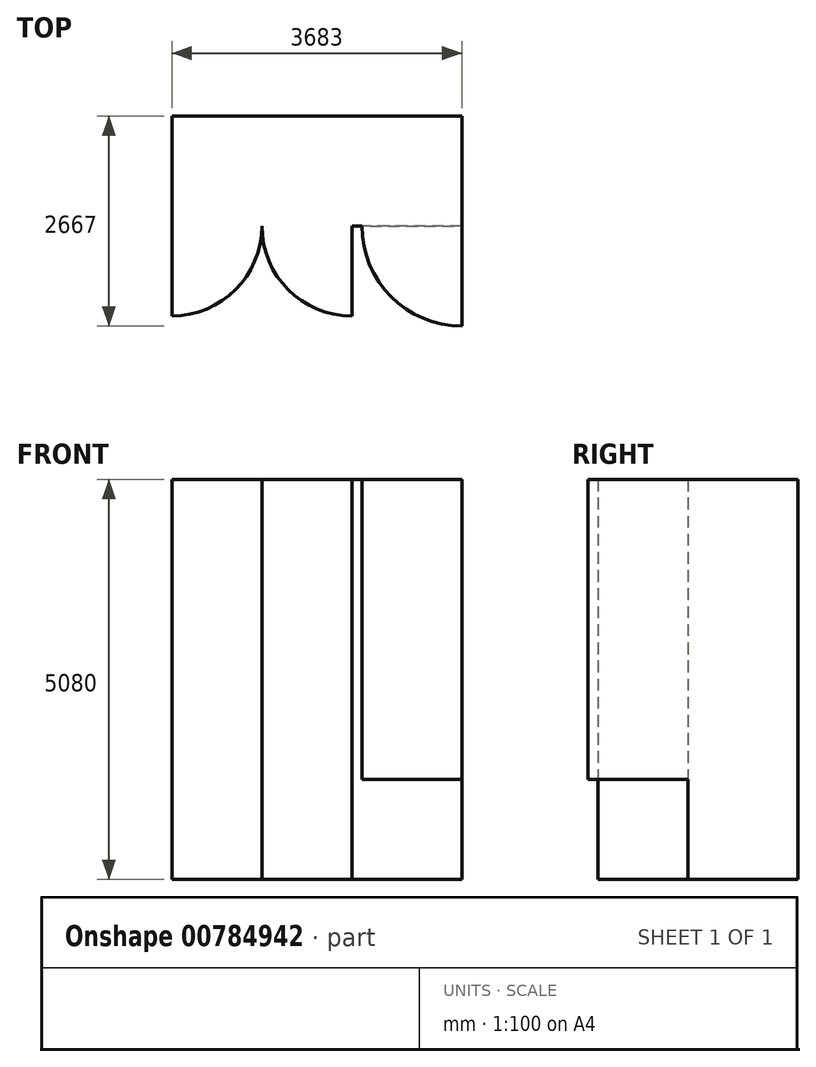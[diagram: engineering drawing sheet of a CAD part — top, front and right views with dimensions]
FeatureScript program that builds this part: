
annotation { "Feature Type Name" : "Feature", "Feature Type Description" : "" }
export const myFeature = defineFeature(function(context is Context, id is Id, definition is map)
    precondition{}
    {
        {
            var Q0;
            Q0=qCreatedBy(makeId("Top.planeOp"),FACE);
            var sketch = newSketch(context, id + "F0", { "sketchPlane" : qUnion([Q0])});
            skLineSegment(sketch, "E0.bottom", {"start": v(0, 0) * mm, "end": v(3683, 0) * mm});
            skLineSegment(sketch, "E0.top", {"start": v(0, 1397) * mm, "end": v(3683, 1397) * mm});
            skLineSegment(sketch, "E0.left", {"start": v(0, 0) * mm, "end": v(0, 1397) * mm});
            skLineSegment(sketch, "E0.right", {"start": v(3683, 0) * mm, "end": v(3683, 1397) * mm});
            skSolve(sketch);
        }
        {
            var Q0;
            Q0 = qSketchRegion(id + "F0", true);
            extrude(context, id + "F1", {"entities" : qUnion([Q0]), "depth" : 5080 * mm, "offsetDistance" : 25.4 * mm});
        }
        {
            var Q0;
            Q0=qCreatedBy(makeId("Top.planeOp"),FACE);
            var sketch = newSketch(context, id + "F2", { "sketchPlane" : qUnion([Q0])});
            skLineSegment(sketch, "E1", {"start": v(0, 0) * mm, "end": v(1143, 0) * mm});
            skSolve(sketch);
        }
        {
            var Q0;
            Q0 = qSketchRegion(id + "F2", true);
            var Q1;
            Q1 = qConstructionFilter(qBodyType(qCreatedBy(id + "F2" ,EDGE), BodyType.WIRE), ConstructionObject.NO);
            var Q2;
            Q2=makeQuery(id+"F1.opExtrude","SWEPT_EDGE",EDGE,{"disambiguationData":[OSD([sQuery(id+"F0.wireOp",EDGE,"E0.bottom"),sQuery(id+"F0.wireOp",EDGE,"E0.left")])]});
            revolve(context, id + "F3", {"bodyType" : ToolBodyType.SURFACE, "surfaceOperationType" : NewSurfaceOperationType.NEW, "entities" : qUnion([Q0]), "surfaceEntities" : qUnion([Q1]), "axis" : qUnion([Q2]), "revolveType" : RevolveType.TWO_DIRECTIONS, "angle" : 90 * degree, "angleBack" : 0 * degree});
        }
        {
            var Q0;
            Q0=qCreatedBy(makeId("Top.planeOp"),FACE);
            var sketch = newSketch(context, id + "F4", { "sketchPlane" : qUnion([Q0])});
            skLineSegment(sketch, "E2", {"start": v(1143, 0) * mm, "end": v(1143, -0.25) * mm});
            skSolve(sketch);
        }
        {
            var Q0;
            Q0 = qSketchRegion(id + "F4", true);
            var Q1;
            Q1 = qConstructionFilter(qBodyType(qCreatedBy(id + "F4" ,EDGE), BodyType.WIRE), ConstructionObject.NO);
            extrude(context, id + "F5", {"entities" : qUnion([Q0]), "bodyType" : ToolBodyType.SURFACE, "surfaceEntities" : qUnion([Q1]), "depth" : 5080 * mm, "offsetDistance" : 25.4 * mm});
        }
        {
            var Q0;
            Q0=makeQuery(id+"F3.opRevolve","SWEPT_BODY",BODY,{"disambiguationData":[OSD([sQuery(id+"F2.wireOp",EDGE,"E1")])]});
            var Q1;
            Q1=makeQuery(id+"F5.opExtrude","SWEPT_FACE",FACE,{"disambiguationData":[OSD([sQuery(id+"F4.wireOp",EDGE,"E2")])]});
            mirror(context, id + "F6", {"entities" : qUnion([Q0]), "mirrorPlane" : qUnion([Q1])});
        }
        {
            var Q0;
            Q0=qCreatedBy(makeId("Top.planeOp"),FACE);
            var sketch = newSketch(context, id + "F7", { "sketchPlane" : qUnion([Q0])});
            skLineSegment(sketch, "E3", {"start": v(3683, 0) * mm, "end": v(2413, 0) * mm});
            skSolve(sketch);
        }
        {
            var Q0;
            Q0 = qConstructionFilter(qBodyType(qCreatedBy(id + "F7" ,EDGE), BodyType.WIRE), ConstructionObject.NO);
            var Q1;
            Q1=makeQuery(id+"F1.opExtrude","SWEPT_EDGE",EDGE,{"disambiguationData":[OSD([sQuery(id+"F0.wireOp",EDGE,"E0.bottom"),sQuery(id+"F0.wireOp",EDGE,"E0.right")])]});
            revolve(context, id + "F8", {"bodyType" : ToolBodyType.SURFACE, "surfaceOperationType" : NewSurfaceOperationType.NEW, "surfaceEntities" : qUnion([Q0]), "axis" : qUnion([Q1]), "revolveType" : RevolveType.TWO_DIRECTIONS, "angle" : 0 * degree, "angleBack" : 270 * degree});
        }
        {
            var Q0;
            Q0=makeQuery(id+"F6.opPattern","COPY",FACE,{"derivedFrom":makeQuery(id+"F3.opRevolve","SWEPT_FACE",FACE,{"disambiguationData":[OSD([sQuery(id+"F2.wireOp",EDGE,"E1")])]}),"instanceName":"1"});
            var Q1;
            Q1=makeQuery(id+"F3.opRevolve","SWEPT_FACE",FACE,{"disambiguationData":[OSD([sQuery(id+"F2.wireOp",EDGE,"E1")])]});
            extrude(context, id + "F9", {"entities" : qUnion([Q0, Q1]), "operationType" : NewBodyOperationType.ADD, "oppositeDirection" : true, "depth" : 5080 * mm, "offsetDistance" : 25.4 * mm});
        }
        {
            var Q0;
            Q0=makeQuery(id+"F8.opRevolve","SWEPT_FACE",FACE,{"disambiguationData":[OSD([sQuery(id+"F7.wireOp",EDGE,"E3")])]});
            extrude(context, id + "F10", {"entities" : qUnion([Q0]), "operationType" : NewBodyOperationType.ADD, "oppositeDirection" : true, "depth" : 5080 * mm, "hasOffset" : true, "offsetDistance" : 1270 * mm, "hasSecondDirection" : true, "secondDirectionOppositeDirection" : false, "secondDirectionDepth" : -1270 * mm});
        }
    });
